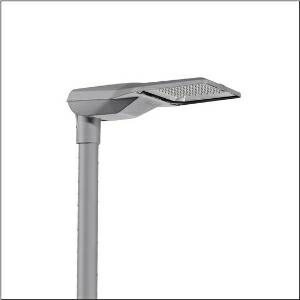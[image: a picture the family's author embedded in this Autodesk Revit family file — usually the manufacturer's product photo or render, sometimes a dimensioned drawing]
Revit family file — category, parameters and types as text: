
# Revit family: streetlight_sl_21_iq_midi___p0_8a_5xe3u31d08nb_0b79
name_source: partatom
category: Lighting Fixtures
units: mm (PartAtom-declared; Revit-internal decimal feet)

## family parameters
Cut with Voids When Loaded = No
Host = Face
Light Source = No
Part Type = Normal
Room Calculation Point = No
Round Connector Dimension = Use Diameter
Shared = No

## types (1)
- --- (1 x LED, 23430 lm, 155.5 W, 3000K)
    Apparent Load = 155 VA
    CIE Flux Codes = 36 69 97 100 100
    Color Rendering = 70
    Color Temperature = 3000K
    Default Elevation = 1800 mm
    Description = Streetlight SL 21 iQ midi, mast luminaire, primary light control with lens, of PMMA, primary optical cover: cover, of toughened safety glass, transparent, light distribution: P0.8a, light emission: direct distribution, primary light characteristic: asymmetric, installation type: post-top, side-entry, LED, High Power LED, rated luminous flux: 23.430lm, luminous efficacy: 151lm/W, light colour: 730, colour temperature: 3000K, control gear: iQ-Comfort, control: pre-setting: linear dimming characteristic, Auto-Match, Temp-Guard, Lumen-Switch, Night-Set, Smart-Wire, Light-Fading, Desk-Remote (wireless, voltage-free reading and setting of iQ features in the workshop via application-optimized NFC function/RFID function), optimised constant luminous flux control (CLO 2.0), mains connection: 230..240V, AC, 50/60Hz, start of lifetime: 156W, end of service life: 162W, reduction: 69W, luminaire housing, of diecast aluminium, powder-coated, SITECO metallic grey (DB 702S), corrosivity category C5 high according to DIN EN ISO 12944, please order mast flange separately, inclination adjustable: 0°, 5°, 10°, 15°, sealing non-destructively replaceable, multi-level sealing system, length: 644mm, width: 335mm, height: 110mm, mast flange for spigot size: 42mm (side-entry): 5XC10008XM4, 60/48mm (side-entry/post-top): 5XC10108XM2, 76/60mm (side-entry/post-top): 5XC10108XM1, mounting height: 4..8m, protection rating (complete): IP66, insulation class (complete): insulation class II (safety insulation), certification: CE, ENEC, ENEC+, VDE, impact resistance: IK10, permissible operating ambient temperature for outdoor applications: -40..+50°C, standard-compliant lighting for roads and squares, packaging unit: 1 piece

Light Distribution: P0.8a
    Height = 111 mm
    Lamp = 1 x LED
    Lamp Light Flux = 23430 lm
    Lamp Power = 155.5 W
    Lamp count = 1
    Length = 644 mm
    Luminous efficacy = 151 lm/W
    Manufacturer = Siteco
    ModVariant = No
    Model = 5XE3U31D08NB
    Number of Poles = 1
    OnlyDefault = Yes
    Power Factor = 1
    Product Name = Streetlight SL 21 iQ midi | P0.8a
    Product group = mast luminaire | pylon top
    ProductGroupID = 6100
    Protection Class = Protection class II
    Protection Degree = IP 66
    RLX_Detail_Level = 1
    RLX_Emergency_Light_Flux = 0 lm
    RLX_Emergency_Type = 0
    RLX_Emergency_Type_DB = No
    RlxData = <blob elided: 90553 chars, md5=66b20e8e>
    Socket = socket
    Standby Power = 0 W
    System Light Flux = 23431 lm
    System Power = 155 W
    Type Comments = factory setting: luminous flux: 100 % | dim-lin: 254 | 823 mA
    Type Image = l_1004298.jpg
    URL = http://relux.com
    VarID = @adj_079297
    Voltage = 0 V
    Weight = 0.00 kg
    Width = 336 mm

## geometry (parser evidence)
native form markers: Blend x4, Sweep x12
no freeform markers — native parametric forms only
